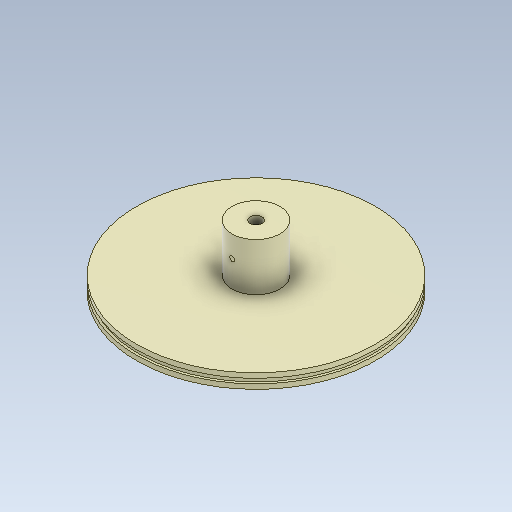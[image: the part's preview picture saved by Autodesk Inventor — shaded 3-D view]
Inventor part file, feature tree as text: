
AUTODESK INVENTOR PART (.ipt)
format: ipt  version: 2020.2 (Build 242310000, 310)  size: 142,848 bytes
history: native  units: in
note: dims shown in document units (in); Inventor stores cm internally (conversion verified against a paired STEP export)
features: extrude x6, sketch x6
ambient origin geometry x8: Origin, YZ Plane, XZ Plane, XY Plane, X Axis, Y Axis, Z Axis, Center Point
bodies: Solid1 (feature_tree)
feature tree (12):
  extrude  "Extrusion1"  Depth=0.0787in TaperAngle=0.0deg
  extrude  "Extrusion2"  Depth=0.0787in TaperAngle=0.0deg
  extrude  "Extrusion3"  Depth=0.0787in TaperAngle=0.0deg
  extrude  "Extrusion4"  Depth=0.7874in TaperAngle=0.0deg
  extrude  "Extrusion5"  Depth=0.9843in TaperAngle=0.0deg
  extrude  "Extrusion6"  Depth=0.7874in TaperAngle=0.0deg
  sketch  "Sketch1"  dims[d0=3.937in d1=0.0787in d2=0.0in]
  sketch  "Sketch2"  dims[d3=3.8583in d4=0.0787in d5=0.0in]
  sketch  "Sketch3"  dims[d6=3.937in d7=0.0787in d8=0.0in]
  sketch  "Sketch4"  dims[d9=0.7874in d10=0.7874in d11=0.0in]
  sketch  "Sketch5"  dims[d12=0.0787in d13=0.9843in d14=0.0in]
  sketch  "Sketch6"  dims[d15=0.1969in d16=0.7874in d17=0.0in]
